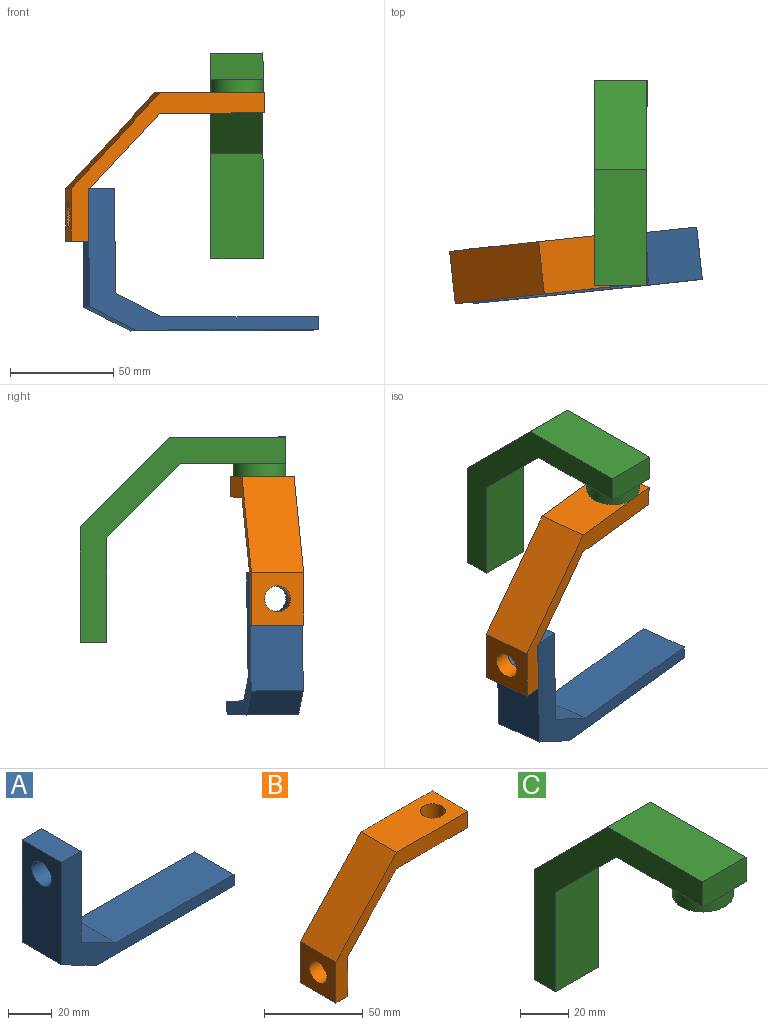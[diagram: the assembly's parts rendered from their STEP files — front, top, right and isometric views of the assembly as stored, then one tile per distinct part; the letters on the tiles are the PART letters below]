
ASSEMBLY  parts=3 mates=2
PART A: 11 faces, bbox 111.5x25.4x68.8 mm
  f0: plane 57.15x25.4mm, normal (-1,0,0), area 1324.9mm2, adj f1,f7,f8,f9,f10
  f1: plane 25.4x22.56mm, normal (-0.46,0,-0.89), area 645.2mm2, adj f0,f2,f8,f9
  f2: plane 88.9x25.4mm, normal (0,0,-1), area 2258.1mm2, adj f1,f3,f8,f9
  f3: plane 25.4x6.35mm, normal (1,0,0), area 161.3mm2, adj f2,f4,f8,f9
  f4: plane 76.2x25.4mm, normal (0,0,1), area 1935.5mm2, adj f3,f5,f8,f9
  f5: plane 25.4x22.56mm, normal (0.46,0,0.89), area 645.2mm2, adj f4,f6,f8,f9
  f6: plane 50.8x25.4mm, normal (1,0,0), area 1163.6mm2, adj f5,f7,f8,f9,f10
  f7: plane 25.4x12.7mm, normal (0,0,1), area 322.6mm2, adj f0,f6,f8,f9
  f8: plane 111.46x68.82mm, normal (0,1,0), area 1501.1mm2, adj f0,f1,f2,f3,f4,f5,f6,f7
  f9: plane 111.46x68.82mm, normal (0,-1,0), area 1501.1mm2, adj f0,f1,f2,f3,f4,f5,f6,f7
  f10: cylinder r=6.35mm len=12.7mm, axis (1,0,0), area 506.7mm2, adj f0,f6
PART B: 12 faces, bbox 94.3x25.4x71.7 mm
  f0: plane 50.8x25.4mm, normal (0,0,-1), area 1163.6mm2, adj f1,f7,f8,f9,f10
  f1: plane 25.4x9.94mm, normal (1,0,-0.02), area 252.5mm2, adj f0,f2,f8,f9
  f2: plane 50.8x25.4mm, normal (0,0,1), area 1163.6mm2, adj f1,f3,f8,f9,f10
  f3: plane 46.26x43.5mm, normal (-0.73,0,0.68), area 1612.9mm2, adj f2,f4,f8,f9
  f4: plane 25.4x25.4mm, normal (-1,0,0), area 518.5mm2, adj f3,f5,f8,f9,f11
  f5: plane 25.4x8.48mm, normal (0,0,-1), area 215.5mm2, adj f4,f6,f8,f9
  f6: plane 25.4x24.72mm, normal (1,0,0), area 501.1mm2, adj f5,f7,f8,f9,f11
  f7: plane 37.01x34.8mm, normal (0.73,0,-0.68), area 1290.3mm2, adj f0,f6,f8,f9
  f8: plane 94.3x71.66mm, normal (0,1,0), area 1097.5mm2, adj f0,f1,f2,f3,f4,f5,f6,f7
  f9: plane 94.3x71.66mm, normal (0,-1,0), area 1097.5mm2, adj f0,f1,f2,f3,f4,f5,f6,f7
  f10: cylinder r=6.35mm len=12.7mm, axis (0,0,-1), area 396.5mm2, adj f0,f2
  f11: cylinder r=6.35mm len=12.7mm, axis (-1,0,0), area 338.5mm2, adj f4,f6
PART C: 14 faces, bbox 25.4x99.4x99.4 mm
  f0: plane 12.7x12.7mm, normal (0,0,-1), area 34.6mm2, adj f5,f10,f12
  f1: plane 12.7x12.7mm, normal (0,0,-1), area 34.6mm2, adj f5,f11,f12
  f2: plane 56.06x25.4mm, normal (0,1,0), area 1423.9mm2, adj f3,f9,f10,f11
  f3: plane 43.36x43.36mm, normal (0,0.71,0.71), area 1557.6mm2, adj f2,f4,f10,f11
  f4: plane 56.06x25.4mm, normal (0,0,1), area 1423.9mm2, adj f3,f5,f10,f11
  f5: plane 25.4x12.7mm, normal (0,-1,0), area 322.6mm2, adj f0,f1,f4,f10,f11
  f6: plane 38.1x25.4mm, normal (0,0,-1), area 714.4mm2, adj f7,f10,f11,f12
  f7: plane 35.92x35.92mm, normal (0,-0.71,-0.71), area 1290.3mm2, adj f6,f8,f10,f11
  f8: plane 50.8x25.4mm, normal (0,-1,0), area 1290.3mm2, adj f7,f9,f10,f11
  f9: plane 25.4x12.7mm, normal (0,0,-1), area 322.6mm2, adj f2,f8,f10,f11
  f10: plane 99.42x99.42mm, normal (1,0,0), area 2069.1mm2, adj f0,f2,f3,f4,f5,f6,f7,f8
  f11: plane 99.42x99.42mm, normal (-1,0,0), area 2069.1mm2, adj f1,f2,f3,f4,f5,f6,f7,f8
  f12: cylinder r=12.7mm len=25.4mm, axis (0,0,1), area 506.7mm2, adj f0,f1,f6,f13
  f13: plane 25.4x25.4mm, normal (0,0,-1), area 506.7mm2, adj f12
PLACE A rot(axis=(-0.15,-0.04,0.99),6.2deg) t=(35.53,-123.77,74.8)mm
PLACE B rot(axis=(0,-0.03,1),6.1deg) t=(35.6,-124.36,72.12)mm
PLACE C rot(axis=(-0.07,-0.87,0.48),0.2deg) t=(23.08,-123.68,71.92)mm fixed
MATE revolute B.f10 <-> C.f12  axis (0,0,-1) through (35.44,0.81,96.24)mm
MATE revolute A.f10 <-> B.f11  axis (-0.99,-0.11,0) through (-37.59,-7.05,37)mm
